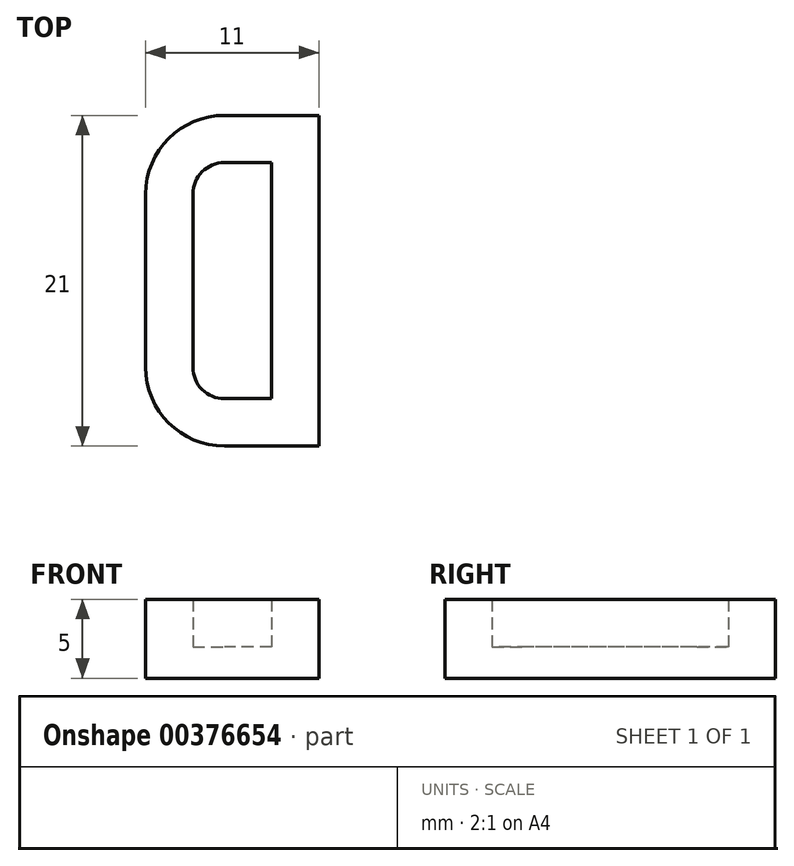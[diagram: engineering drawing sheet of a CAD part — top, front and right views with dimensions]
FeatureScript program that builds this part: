
annotation { "Feature Type Name" : "Feature", "Feature Type Description" : "" }
export const myFeature = defineFeature(function(context is Context, id is Id, definition is map)
    precondition{}
    {
        {
            var Q0;
            Q0=qCreatedBy(makeId("Top.planeOp"),FACE);
            var sketch = newSketch(context, id + "F0", { "sketchPlane" : qUnion([Q0])});
            skLineSegment(sketch, "E0.bottom", {"start": v(2.5, 7.5) * mm, "end": v(-2.5, 7.5) * mm});
            skLineSegment(sketch, "E0.top", {"start": v(2.5, -7.5) * mm, "end": v(-2.5, -7.5) * mm});
            skLineSegment(sketch, "E0.left", {"start": v(2.5, 7.5) * mm, "end": v(2.5, -7.5) * mm});
            skLineSegment(sketch, "E0.right", {"start": v(-2.5, 7.5) * mm, "end": v(-2.5, -7.5) * mm});
            skPoint(sketch, "E0.middle", {"position": v(0, 0) * mm});
            skLineSegment(sketch, "E1.bottom", {"start": v(5.5, 10.5) * mm, "end": v(-5.5, 10.5) * mm});
            skLineSegment(sketch, "E1.top", {"start": v(5.5, -10.5) * mm, "end": v(-5.5, -10.5) * mm});
            skLineSegment(sketch, "E1.left", {"start": v(5.5, 10.5) * mm, "end": v(5.5, -10.5) * mm});
            skLineSegment(sketch, "E1.right", {"start": v(-5.5, 10.5) * mm, "end": v(-5.5, -10.5) * mm});
            skSolve(sketch);
        }
        {
            var Q0;
            Q0=makeQuery(id+"F0.imprint","IMPRINT",FACE,{"disambiguationData":[TD([[makeQuery(id+"F0.imprint","IMPRINT",EDGE,{"derivedFrom":sQuery(id+"F0.wireOp",EDGE,"E0.bottom")}),-1.0]])]});
            extrude(context, id + "F1", {"entities" : qUnion([Q0]), "depth" : 3 * mm});
        }
        {
            var Q0;
            Q0=makeQuery(id+"F1.opExtrude","CAP_FACE",FACE,{"disambiguationData":[OSD([sQuery(id+"F0.wireOp",EDGE,"E0.bottom"),sQuery(id+"F0.wireOp",EDGE,"E0.top"),sQuery(id+"F0.wireOp",EDGE,"E0.left"),sQuery(id+"F0.wireOp",EDGE,"E0.right"),sQuery(id+"F0.wireOp",EDGE,"E1.bottom"),sQuery(id+"F0.wireOp",EDGE,"E1.top"),sQuery(id+"F0.wireOp",EDGE,"E1.left"),sQuery(id+"F0.wireOp",EDGE,"E1.right")])],"isStart":true});
            var sketch = newSketch(context, id + "F2", { "sketchPlane" : qUnion([Q0])});
            skLineSegment(sketch, "E2.bottom", {"start": v(-5.5, 10.5) * mm, "end": v(5.5, 10.5) * mm});
            skLineSegment(sketch, "E2.top", {"start": v(-5.5, -10.5) * mm, "end": v(5.5, -10.5) * mm});
            skLineSegment(sketch, "E2.left", {"start": v(-5.5, 10.5) * mm, "end": v(-5.5, -10.5) * mm});
            skLineSegment(sketch, "E2.right", {"start": v(5.5, 10.5) * mm, "end": v(5.5, -10.5) * mm});
            skSolve(sketch);
        }
        {
            var Q0;
            Q0 = qSketchRegion(id + "F2", true);
            extrude(context, id + "F3", {"entities" : qUnion([Q0]), "operationType" : NewBodyOperationType.ADD, "depth" : 2 * mm});
        }
        {
            var Q0;
            Q0=makeQuery(id+"F1.opExtrude","SWEPT_EDGE",EDGE,{"disambiguationData":[OSD([sQuery(id+"F0.wireOp",EDGE,"E0.top"),sQuery(id+"F0.wireOp",EDGE,"E0.right")])]});
            var Q1;
            Q1=makeQuery(id+"F1.opExtrude","SWEPT_EDGE",EDGE,{"disambiguationData":[OSD([sQuery(id+"F0.wireOp",EDGE,"E0.bottom"),sQuery(id+"F0.wireOp",EDGE,"E0.right")])]});
            fillet(context, id + "F4", {"entities" : qUnion([Q0, Q1]), "radius" : 2 * mm, "tangentPropagation" : true, "allowEdgeOverflow" : false});
        }
        {
            var Q0;
            Q0=makeQuery(id+"F3.boolean.opBoolean","MERGE",EDGE,{"derivedFrom":[makeQuery(id+"F1.opExtrude","SWEPT_EDGE",EDGE,{"disambiguationData":[OSD([sQuery(id+"F0.wireOp",EDGE,"E1.top"),sQuery(id+"F0.wireOp",EDGE,"E1.right")])]}),makeQuery(id+"F3.opExtrude","SWEPT_EDGE",EDGE,{"disambiguationData":[OSD([sQuery(id+"F2.wireOp",EDGE,"E2.bottom"),sQuery(id+"F2.wireOp",EDGE,"E2.left")])]})]});
            var Q1;
            Q1=makeQuery(id+"F3.boolean.opBoolean","MERGE",EDGE,{"derivedFrom":[makeQuery(id+"F1.opExtrude","SWEPT_EDGE",EDGE,{"disambiguationData":[OSD([sQuery(id+"F0.wireOp",EDGE,"E1.bottom"),sQuery(id+"F0.wireOp",EDGE,"E1.right")])]}),makeQuery(id+"F3.opExtrude","SWEPT_EDGE",EDGE,{"disambiguationData":[OSD([sQuery(id+"F2.wireOp",EDGE,"E2.top"),sQuery(id+"F2.wireOp",EDGE,"E2.left")])]})]});
            fillet(context, id + "F5", {"entities" : qUnion([Q0, Q1]), "radius" : 5 * mm, "tangentPropagation" : true, "allowEdgeOverflow" : false});
        }
    });
